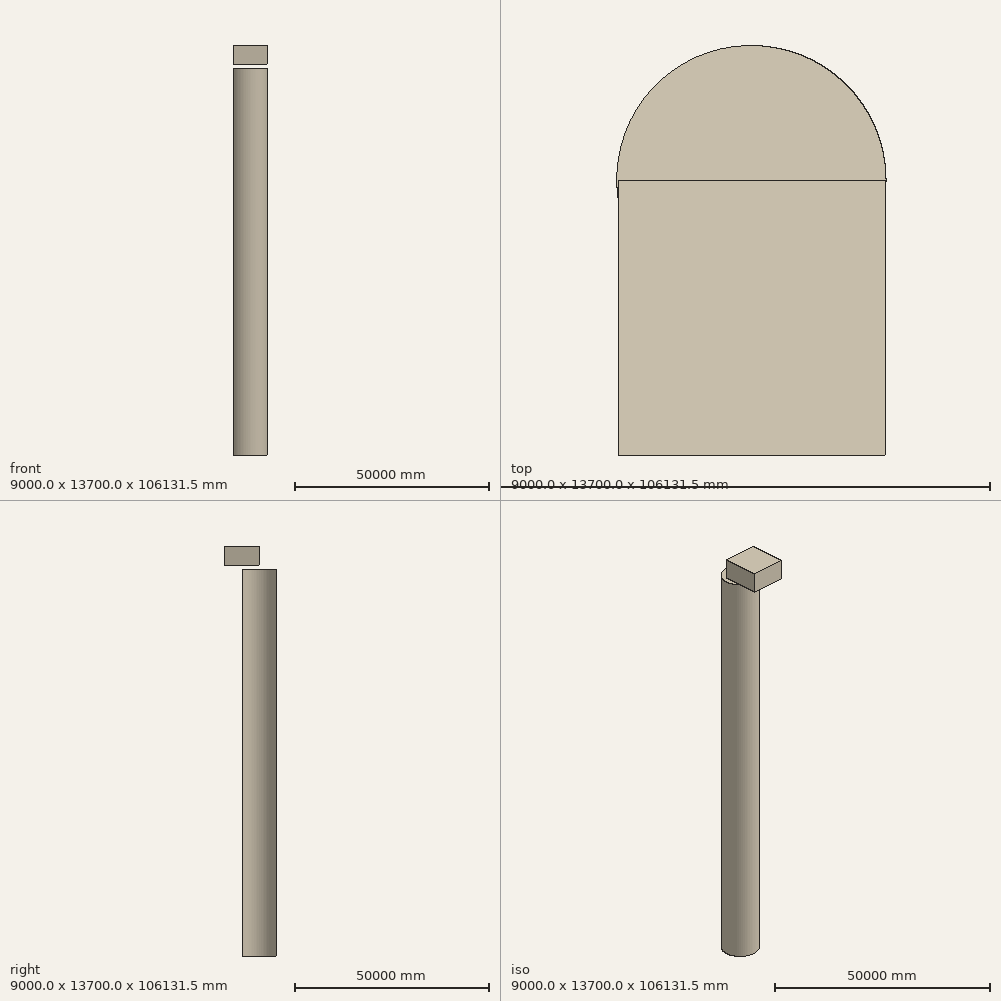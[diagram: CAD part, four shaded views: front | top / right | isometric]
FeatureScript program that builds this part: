
annotation { "Feature Type Name" : "Feature", "Feature Type Description" : "" }
export const myFeature = defineFeature(function(context is Context, id is Id, definition is map)
    precondition{}
    {
        {
            var Q0;
            Q0=qCreatedBy(makeId("Top.planeOp"),FACE);
            var sketch = newSketch(context, id + "F0", { "sketchPlane" : qUnion([Q0])});
            skCircle(sketch, "E0", {"center": v(0, 0) * mm, "radius": 4000 * mm});
            skSolve(sketch);
        }
        {
            var Q0;
            Q0=makeQuery(id+"F0.imprint","IMPRINT",FACE,{"disambiguationData":[TD([[makeQuery(id+"F0.imprint","IMPRINT",EDGE,{"derivedFrom":sQuery(id+"F0.wireOp",EDGE,"E0")}),1.0]])]});
            var sketch = newSketch(context, id + "F1", { "sketchPlane" : qUnion([Q0])});
            skCircle(sketch, "E1", {"center": v(0, 0) * mm, "radius": 4500 * mm});
            skSolve(sketch);
        }
        {
            var Q0;
            Q0=makeQuery(id+"F1.imprint","IMPRINT",FACE,{"disambiguationData":[TD([[makeQuery(id+"F1.imprint","IMPRINT",EDGE,{"derivedFrom":sQuery(id+"F1.wireOp",EDGE,"E1")}),1.0]])]});
            extrude(context, id + "F2", {"entities" : qUnion([Q0]), "depth" : 100000 * mm, "offsetDistance" : 25 * mm});
        }
        {
            var Q0;
            Q0=makeQuery(id+"F2.opExtrude","CAP_FACE",FACE,{"disambiguationData":[OSD([sQuery(id+"F0.wireOp",EDGE,"E0"),sQuery(id+"F1.wireOp",EDGE,"E1")])],"isStart":false});
            var sketch = newSketch(context, id + "F3", { "sketchPlane" : qUnion([Q0])});
            skCircle(sketch, "E2", {"center": v(0, 0) * mm, "radius": 4500 * mm});
            skSolve(sketch);
        }
        {
            var Q0;
            Q0 = qSketchRegion(id + "F3", true);
            extrude(context, id + "F4", {"entities" : qUnion([Q0]), "operationType" : NewBodyOperationType.ADD, "depth" : 200 * mm, "offsetDistance" : 25 * mm});
        }
        {
            var Q0;
            Q0=qCreatedBy(makeId("Front.planeOp"),FACE);
            var sketch = newSketch(context, id + "F5", { "sketchPlane" : qUnion([Q0])});
            skLineSegment(sketch, "E3.bottom", {"start": v(-4453.4, 101201.92) * mm, "end": v(4486.43, 101201.92) * mm});
            skLineSegment(sketch, "E3.top", {"start": v(-4453.4, 106131.46) * mm, "end": v(4486.43, 106131.46) * mm});
            skLineSegment(sketch, "E3.left", {"start": v(-4453.4, 101201.92) * mm, "end": v(-4453.4, 106131.46) * mm});
            skLineSegment(sketch, "E3.right", {"start": v(4486.43, 101201.92) * mm, "end": v(4486.43, 106131.46) * mm});
            skSolve(sketch);
        }
        {
            var Q0;
            Q0=makeQuery(id+"F5.imprint","IMPRINT",FACE,{"disambiguationData":[TD([[makeQuery(id+"F5.imprint","IMPRINT",EDGE,{"derivedFrom":sQuery(id+"F5.wireOp",EDGE,"E3.bottom")}),1.0]])]});
            extrude(context, id + "F6", {"entities" : qUnion([Q0]), "operationType" : NewBodyOperationType.ADD, "depth" : 9200 * mm, "offsetDistance" : 25 * mm});
        }
    });
